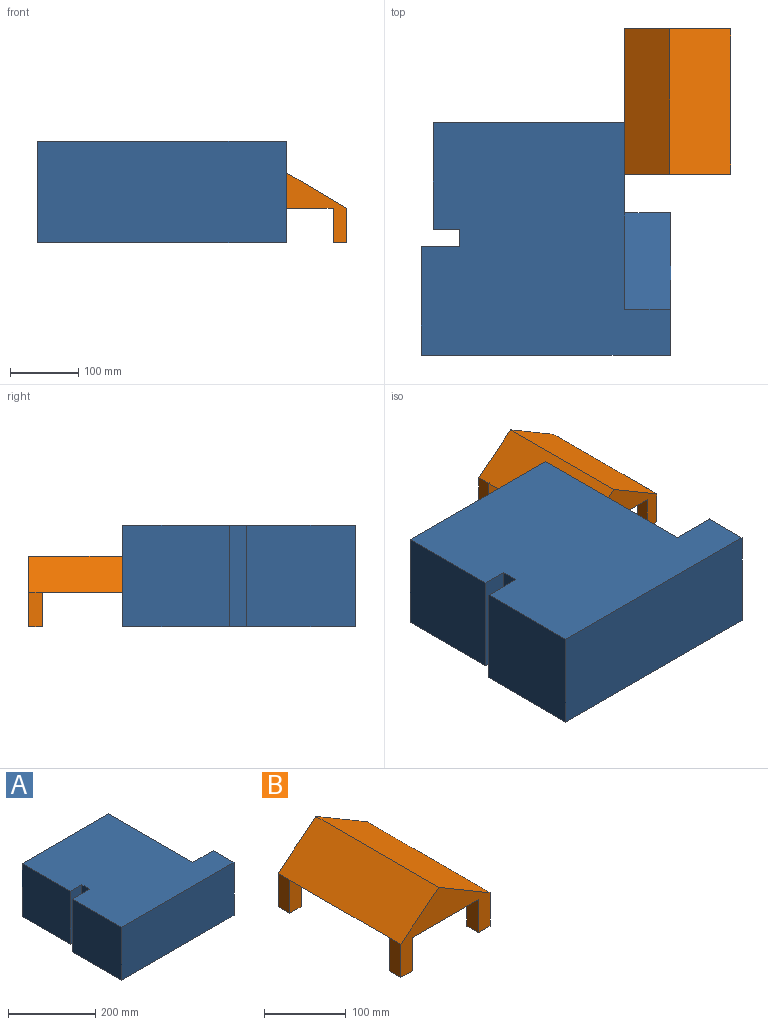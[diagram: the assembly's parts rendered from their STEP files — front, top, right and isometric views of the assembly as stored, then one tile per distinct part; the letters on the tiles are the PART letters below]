
ASSEMBLY  parts=2 mates=1
PART A: 17 faces, bbox 364.2x339.7x148 mm
  f0: plane 272.64x147.83mm, normal (1,0,0), area 29840.1mm2, adj f2,f3,f4,f14
  f1: plane 91.94x0.11mm, normal (1,0,0), area 5mm2, adj f8,f11,f15
  f2: plane 363.6x339.66mm, normal (0,0,1), area 101265.7mm2, adj f0,f4,f5,f6,f7,f8,f9,f10
  f3: plane 346.61x180.7mm, normal (0,0,-1), area 52901.9mm2, adj f0,f4,f5,f6,f7,f8,f14,f16
  f4: plane 279.61x147.83mm, normal (0,1,0), area 41335.8mm2, adj f0,f2,f3,f5
  f5: plane 155.7x147.83mm, normal (-1,0,0), area 23017.6mm2, adj f2,f3,f4,f6
  f6: plane 147.83x38mm, normal (0,-1,0), area 5617.7mm2, adj f2,f3,f5,f7
  f7: plane 147.83x25mm, normal (-1,0,0), area 3695.8mm2, adj f2,f3,f6,f8
  f8: plane 364.15x148mm, normal (0,1,0), area 8264.3mm2, adj f1,f2,f3,f7,f9,f11,f15,f16
  f9: plane 158.96x148mm, normal (-1,0,0), area 23526.8mm2, adj f2,f8,f10,f11
  f10: plane 363.6x148mm, normal (0,-1,0), area 53812mm2, adj f2,f9,f11,f12
  f11: plane 363.6x158.96mm, normal (0,0,-1), area 51689.8mm2, adj f1,f8,f9,f10,f12,f15
  f12: plane 148x67.02mm, normal (1,0,0), area 9919.3mm2, adj f2,f10,f11,f13
  f13: plane 148x0.56mm, normal (0,-1,0), area 82.5mm2, adj f12,f14,f15,f16
  f14: plane 147.83x141.59mm, normal (0,0.72,0.69), area 13714.7mm2, adj f0,f2,f3,f13,f16
  f15: plane 91.94x67mm, normal (0,0,-1), area 6160.1mm2, adj f1,f8,f11,f13,f16
  f16: plane 148x141.59mm, normal (1,0,0), area 10475.9mm2, adj f3,f8,f13,f14,f15
PART B: 21 faces, bbox 154.8x213x102.7 mm
  f0: plane 213x154.82mm, normal (0,0,-1), area 31376.5mm2, adj f1,f2,f3,f4,f6,f7,f9,f11
  f1: plane 213x65.87mm, normal (-0.62,0,0.78), area 17968.6mm2, adj f0,f2,f3,f4,f5,f14
  f2: plane 213x88.95mm, normal (0.51,0,0.86), area 22021mm2, adj f0,f1,f3,f4,f10,f17
  f3: plane 154.82x102.7mm, normal (0,-1,0), area 6079.4mm2, adj f0,f1,f2,f5,f7,f8,f10,f11
  f4: plane 154.82x102.7mm, normal (0,1,0), area 6079.4mm2, adj f0,f1,f2,f14,f15,f16,f17,f19
  f5: plane 50x20mm, normal (-1,0,0), area 1000mm2, adj f1,f3,f6,f8
  f6: plane 50x20mm, normal (0,1,0), area 1000mm2, adj f0,f5,f7,f8
  f7: plane 50x20mm, normal (1,0,0), area 1000mm2, adj f0,f3,f6,f8
  f8: plane 20x20mm, normal (0,0,-1), area 400mm2, adj f3,f5,f6,f7
  f9: plane 50x20mm, normal (0,1,0), area 1000mm2, adj f0,f10,f11,f12
  f10: plane 50x20mm, normal (1,0,0), area 1000mm2, adj f2,f3,f9,f12
  f11: plane 50x20mm, normal (-1,0,0), area 1000mm2, adj f0,f3,f9,f12
  f12: plane 20x20mm, normal (0,0,-1), area 400mm2, adj f3,f9,f10,f11
  f13: plane 50x20mm, normal (0,-1,0), area 1000mm2, adj f0,f14,f15,f16
  f14: plane 50x20mm, normal (-1,0,0), area 1000mm2, adj f1,f4,f13,f16
  f15: plane 50x20mm, normal (1,0,0), area 1000mm2, adj f0,f4,f13,f16
  f16: plane 20x20mm, normal (0,0,-1), area 400mm2, adj f4,f13,f14,f15
  f17: plane 50x20mm, normal (1,0,0), area 1000mm2, adj f2,f4,f18,f20
  f18: plane 50x20mm, normal (0,-1,0), area 1000mm2, adj f0,f17,f19,f20
  f19: plane 50x20mm, normal (-1,0,0), area 1000mm2, adj f0,f4,f18,f20
  f20: plane 20x20mm, normal (0,0,-1), area 400mm2, adj f4,f17,f18,f19
PLACE A t=(-126.72,-61.85,-23.34)mm
PLACE B t=(53.99,100.62,-19.72)mm
MATE fastened B.f5 <-> A.f0  axis (-1,0,0) through (-11.88,-102.38,-96.12)mm
